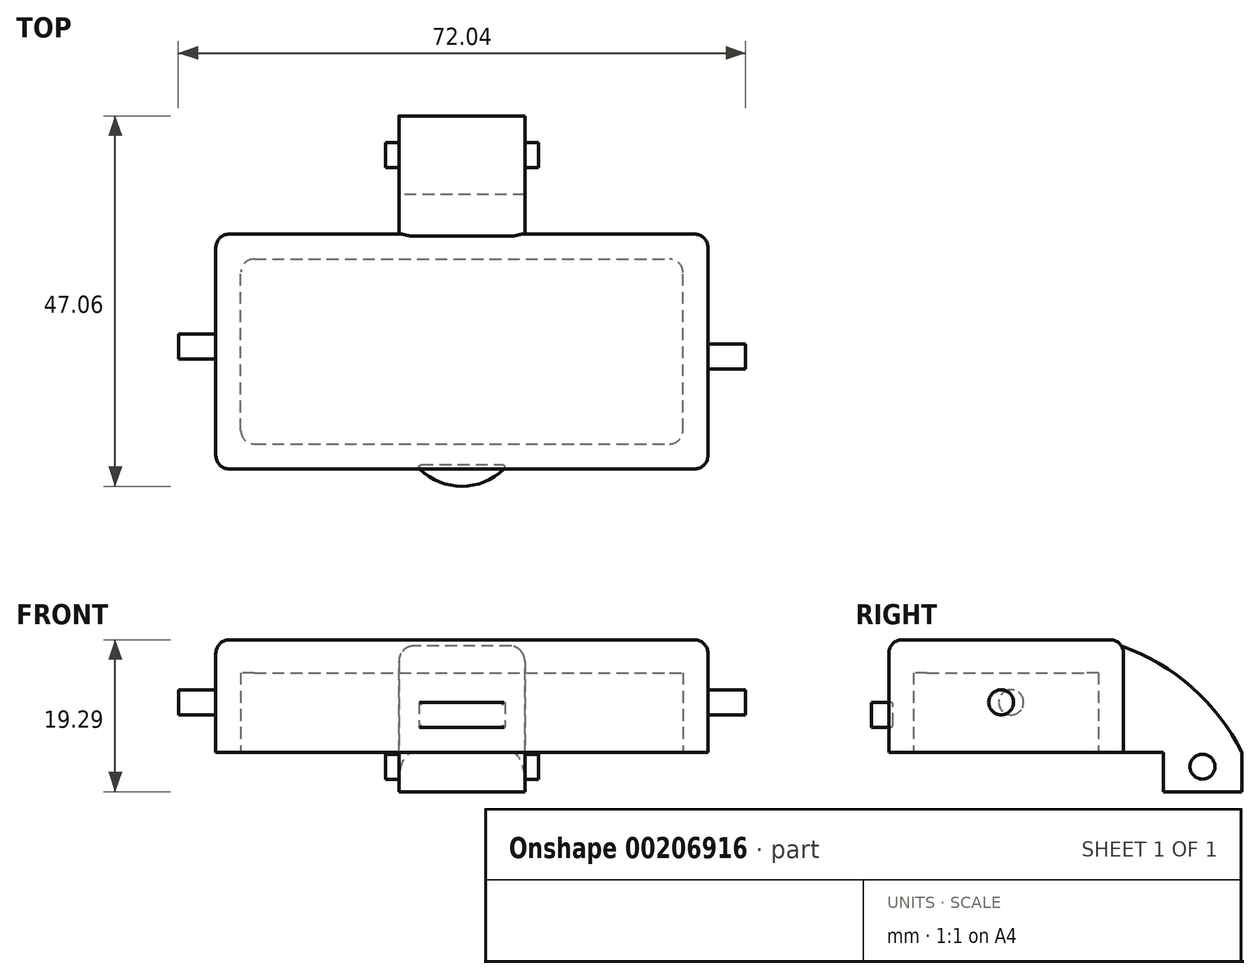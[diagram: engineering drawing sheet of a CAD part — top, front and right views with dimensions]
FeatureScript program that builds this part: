
annotation { "Feature Type Name" : "Feature", "Feature Type Description" : "" }
export const myFeature = defineFeature(function(context is Context, id is Id, definition is map)
    precondition{}
    {
        {
            var Q0;
            Q0=qCreatedBy(makeId("Top.planeOp"),FACE);
            var sketch = newSketch(context, id + "F0", { "sketchPlane" : qUnion([Q0])});
            skLineSegment(sketch, "E0.bottom", {"start": v(-31.25, 14.92) * mm, "end": v(31.25, 14.92) * mm});
            skLineSegment(sketch, "E0.top", {"start": v(-31.25, -14.92) * mm, "end": v(31.25, -14.92) * mm});
            skLineSegment(sketch, "E0.left", {"start": v(-31.25, 14.92) * mm, "end": v(-31.25, -14.92) * mm});
            skLineSegment(sketch, "E0.right", {"start": v(31.25, 14.92) * mm, "end": v(31.25, -14.92) * mm});
            skPoint(sketch, "E0.middle", {"position": v(0, 0) * mm});
            skSolve(sketch);
        }
        {
            var Q0;
            Q0=qSketchRegion(id+"F0",true);
            extrude(context, id + "F1", {"entities" : qUnion([Q0]), "depth" : 14.29 * mm});
        }
        {
            var Q0;
            Q0=qCreatedBy(makeId("Top.planeOp"),FACE);
            cPlane(context, id + "F2", {"entities" : qUnion([Q0]), "cplaneType" : CPlaneType.OFFSET, "offset" : 3.17 * mm, "width" : 152.4 * mm, "height" : 152.4 * mm});
        }
        {
            var Q0;
            Q0=qCreatedBy(id+"F2.planeOp",FACE);
            var sketch = newSketch(context, id + "F3", { "sketchPlane" : qUnion([Q0])});
            skPoint(sketch, "E1", {"position": v(-5.85, -14.38) * mm});
            skPoint(sketch, "E2", {"position": v(5.85, -14.38) * mm});
            skArc(sketch, "E3", {"start": v(-5.85, -14.38) * mm, "mid": v(0, -17.12) * mm, "end": v(5.85, -14.38) * mm});
            skLineSegment(sketch, "E4", {"start": v(-5.85, -14.38) * mm, "end": v(5.85, -14.38) * mm});
            skSolve(sketch);
        }
        {
            var Q0;
            Q0=qSketchRegion(id+"F3",true);
            extrude(context, id + "F4", {"entities" : qUnion([Q0]), "depth" : 3.17 * mm});
        }
        {
            var Q0;
            {var subQ0=sQuery(id+"F3.wireOp",EDGE,"E4");var subQ1=sQuery(id+"F3.wireOp",EDGE,"E3");Q0=makeQuery(id+"F4.opExtrude","SWEPT_EDGE",EDGE,{"disambiguationData":[OSD([subQ1,subQ0]),TDD([makeQuery(id+"F3.imprint","INTERSECT",VERTEX,{"disambiguationData":[OD(1.0)],"derivedFrom":[subQ1,subQ0]})])]});}
            var Q1;
            {var subQ0=sQuery(id+"F3.wireOp",EDGE,"E4");var subQ1=sQuery(id+"F3.wireOp",EDGE,"E3");Q1=makeQuery(id+"F4.opExtrude","SWEPT_EDGE",EDGE,{"disambiguationData":[OSD([subQ1,subQ0]),TDD([makeQuery(id+"F3.imprint","INTERSECT",VERTEX,{"disambiguationData":[OD(0.0)],"derivedFrom":[subQ1,subQ0]})])]});}
            var Q2;
            Q2=makeQuery(id+"F4.opExtrude","CAP_EDGE",EDGE,{"disambiguationData":[OSD([sQuery(id+"F3.wireOp",EDGE,"E4")])],"isStart":false});
            var Q3;
            Q3=makeQuery(id+"F4.opExtrude","CAP_EDGE",EDGE,{"disambiguationData":[OSD([sQuery(id+"F3.wireOp",EDGE,"E4")])],"isStart":true});
            fillet(context, id + "F5", {"entities" : qUnion([Q0, Q1, Q2, Q3]), "radius" : 0.32 * mm, "tangentPropagation" : true, "allowEdgeOverflow" : false});
        }
        {
            var Q0;
            Q0=makeQuery(id+"F1.opExtrude","SWEPT_EDGE",EDGE,{"disambiguationData":[OSD([sQuery(id+"F0.wireOp",EDGE,"E0.top"),sQuery(id+"F0.wireOp",EDGE,"E0.left")])]});
            var Q1;
            Q1=makeQuery(id+"F1.opExtrude","SWEPT_EDGE",EDGE,{"disambiguationData":[OSD([sQuery(id+"F0.wireOp",EDGE,"E0.top"),sQuery(id+"F0.wireOp",EDGE,"E0.right")])]});
            var Q2;
            Q2=makeQuery(id+"F1.opExtrude","SWEPT_EDGE",EDGE,{"disambiguationData":[OSD([sQuery(id+"F0.wireOp",EDGE,"E0.bottom"),sQuery(id+"F0.wireOp",EDGE,"E0.right")])]});
            var Q3;
            Q3=makeQuery(id+"F1.opExtrude","SWEPT_EDGE",EDGE,{"disambiguationData":[OSD([sQuery(id+"F0.wireOp",EDGE,"E0.bottom"),sQuery(id+"F0.wireOp",EDGE,"E0.left")])]});
            var Q4;
            Q4=makeQuery(id+"F1.opExtrude","CAP_FACE",FACE,{"disambiguationData":[OSD([sQuery(id+"F0.wireOp",EDGE,"E0.bottom"),sQuery(id+"F0.wireOp",EDGE,"E0.top"),sQuery(id+"F0.wireOp",EDGE,"E0.left"),sQuery(id+"F0.wireOp",EDGE,"E0.right")])],"isStart":false});
            fillet(context, id + "F6", {"entities" : qUnion([Q0, Q1, Q2, Q3, Q4]), "radius" : 1.71 * mm, "tangentPropagation" : true, "allowEdgeOverflow" : false});
        }
        {
            var Q0;
            Q0=makeQuery(id+"F1.opExtrude","CAP_FACE",FACE,{"disambiguationData":[OSD([sQuery(id+"F0.wireOp",EDGE,"E0.bottom"),sQuery(id+"F0.wireOp",EDGE,"E0.top"),sQuery(id+"F0.wireOp",EDGE,"E0.left"),sQuery(id+"F0.wireOp",EDGE,"E0.right")])],"isStart":true});
            var sketch = newSketch(context, id + "F7", { "sketchPlane" : qUnion([Q0])});
            skLineSegment(sketch, "E5.bottom", {"start": v(-28.08, 11.75) * mm, "end": v(28.08, 11.75) * mm});
            skLineSegment(sketch, "E5.top", {"start": v(-28.08, -11.75) * mm, "end": v(28.08, -11.75) * mm});
            skLineSegment(sketch, "E5.left", {"start": v(-28.08, 11.75) * mm, "end": v(-28.08, -11.75) * mm});
            skLineSegment(sketch, "E5.right", {"start": v(28.08, 11.75) * mm, "end": v(28.08, -11.75) * mm});
            skSolve(sketch);
        }
        {
            var Q0;
            Q0=makeQuery(id+"F7.imprint","IMPRINT",FACE,{"disambiguationData":[TD([[makeQuery(id+"F7.imprint","IMPRINT",EDGE,{"derivedFrom":sQuery(id+"F7.wireOp",EDGE,"E5.bottom")}),-1.0]])]});
            extrude(context, id + "F8", {"entities" : qUnion([Q0]), "operationType" : NewBodyOperationType.REMOVE, "oppositeDirection" : true, "depth" : 10.1 * mm});
        }
        {
            var Q0;
            Q0=makeQuery(id+"F8.boolean.opBoolean","COPY",EDGE,{"derivedFrom":makeQuery(id+"F8.opExtrude","SWEPT_EDGE",EDGE,{"disambiguationData":[OSD([sQuery(id+"F7.wireOp",EDGE,"E5.top"),sQuery(id+"F7.wireOp",EDGE,"E5.left")])]})});
            var Q1;
            Q1=makeQuery(id+"F8.boolean.opBoolean","COPY",EDGE,{"derivedFrom":makeQuery(id+"F8.opExtrude","SWEPT_EDGE",EDGE,{"disambiguationData":[OSD([sQuery(id+"F7.wireOp",EDGE,"E5.bottom"),sQuery(id+"F7.wireOp",EDGE,"E5.left")])]})});
            var Q2;
            Q2=makeQuery(id+"F8.boolean.opBoolean","COPY",EDGE,{"derivedFrom":makeQuery(id+"F8.opExtrude","SWEPT_EDGE",EDGE,{"disambiguationData":[OSD([sQuery(id+"F7.wireOp",EDGE,"E5.bottom"),sQuery(id+"F7.wireOp",EDGE,"E5.right")])]})});
            var Q3;
            Q3=makeQuery(id+"F8.boolean.opBoolean","COPY",EDGE,{"derivedFrom":makeQuery(id+"F8.opExtrude","SWEPT_EDGE",EDGE,{"disambiguationData":[OSD([sQuery(id+"F7.wireOp",EDGE,"E5.top"),sQuery(id+"F7.wireOp",EDGE,"E5.right")])]})});
            fillet(context, id + "F9", {"entities" : qUnion([Q0, Q1, Q2, Q3]), "radius" : 1.71 * mm, "tangentPropagation" : true, "allowEdgeOverflow" : false});
        }
        {
            var Q0;
            Q0=makeQuery(id+"F1.opExtrude","SWEPT_FACE",FACE,{"disambiguationData":[OSD([sQuery(id+"F0.wireOp",EDGE,"E0.right")])]});
            var sketch = newSketch(context, id + "F10", { "sketchPlane" : qUnion([Q0])});
            skCircle(sketch, "E6", {"center": v(-0.63, 6.35) * mm, "radius": 1.59 * mm});
            skSolve(sketch);
        }
        {
            var Q0;
            Q0=makeQuery(id+"F10.imprint","IMPRINT",FACE,{"disambiguationData":[TD([[makeQuery(id+"F10.imprint","IMPRINT",EDGE,{"derivedFrom":sQuery(id+"F10.wireOp",EDGE,"E6")}),1.0]])]});
            extrude(context, id + "F11", {"entities" : qUnion([Q0]), "operationType" : NewBodyOperationType.ADD, "depth" : 4.76 * mm});
        }
        {
            var Q0;
            Q0=makeQuery(id+"F1.opExtrude","SWEPT_FACE",FACE,{"disambiguationData":[OSD([sQuery(id+"F0.wireOp",EDGE,"E0.left")])]});
            var sketch = newSketch(context, id + "F12", { "sketchPlane" : qUnion([Q0])});
            skCircle(sketch, "E7", {"center": v(-0.63, 6.35) * mm, "radius": 1.59 * mm});
            skSolve(sketch);
        }
        {
            var Q0;
            Q0=makeQuery(id+"F12.imprint","IMPRINT",FACE,{"disambiguationData":[TD([[makeQuery(id+"F12.imprint","IMPRINT",EDGE,{"derivedFrom":sQuery(id+"F12.wireOp",EDGE,"E7")}),1.0]])]});
            extrude(context, id + "F13", {"entities" : qUnion([Q0]), "operationType" : NewBodyOperationType.ADD, "depth" : 4.76 * mm});
        }
        {
            var Q0;
            Q0=qCreatedBy(makeId("Right.planeOp"),FACE);
            var sketch = newSketch(context, id + "F14", { "sketchPlane" : qUnion([Q0])});
            skPoint(sketch, "E8", {"position": v(11.94, 14.29) * mm});
            skLineSegment(sketch, "E9", {"start": v(11.94, 0) * mm, "end": v(19.94, 0) * mm});
            skLineSegment(sketch, "E10", {"start": v(19.94, 0) * mm, "end": v(19.94, -5) * mm});
            skLineSegment(sketch, "E11", {"start": v(19.94, -5) * mm, "end": v(29.94, -5) * mm});
            skLineSegment(sketch, "E12", {"start": v(29.94, -5) * mm, "end": v(29.94, 0) * mm});
            skArc(sketch, "E13", {"start": v(29.94, 0) * mm, "mid": v(22.53, 9.15) * mm, "end": v(11.94, 14.29) * mm});
            skLineSegment(sketch, "E14", {"start": v(11.94, 14.29) * mm, "end": v(11.94, 0) * mm});
            skSolve(sketch);
        }
        {
            var Q0;
            Q0=makeQuery(id+"F14.imprint","IMPRINT",FACE,{"disambiguationData":[TD([[makeQuery(id+"F14.imprint","IMPRINT",EDGE,{"derivedFrom":sQuery(id+"F14.wireOp",EDGE,"E9")}),1.0]])]});
            extrude(context, id + "F15", {"entities" : qUnion([Q0]), "operationType" : NewBodyOperationType.ADD, "endBound" : BoundingType.SYMMETRIC, "depth" : 16 * mm});
        }
        {
            var Q0;
            Q0=makeQuery(id+"F15.opExtrude","CAP_EDGE",EDGE,{"disambiguationData":[OSD([sQuery(id+"F14.wireOp",EDGE,"E13")])],"isStart":false});
            var Q1;
            Q1=makeQuery(id+"F15.opExtrude","CAP_EDGE",EDGE,{"disambiguationData":[OSD([sQuery(id+"F14.wireOp",EDGE,"E13")])],"isStart":true});
            fillet(context, id + "F16", {"entities" : qUnion([Q0, Q1]), "radius" : 1.71 * mm, "tangentPropagation" : true, "allowEdgeOverflow" : false});
        }
        {
            var Q0;
            Q0=makeQuery(id+"F15.opExtrude","CAP_FACE",FACE,{"disambiguationData":[OSD([sQuery(id+"F14.wireOp",EDGE,"E9"),sQuery(id+"F14.wireOp",EDGE,"E10"),sQuery(id+"F14.wireOp",EDGE,"E11"),sQuery(id+"F14.wireOp",EDGE,"E12"),sQuery(id+"F14.wireOp",EDGE,"E13"),sQuery(id+"F14.wireOp",EDGE,"E14")])],"isStart":false});
            var sketch = newSketch(context, id + "F17", { "sketchPlane" : qUnion([Q0])});
            skCircle(sketch, "E15", {"center": v(24.94, -1.82) * mm, "radius": 1.59 * mm});
            skSolve(sketch);
        }
        {
            var Q0;
            Q0=makeQuery(id+"F17.imprint","IMPRINT",FACE,{"disambiguationData":[TD([[makeQuery(id+"F17.imprint","IMPRINT",EDGE,{"derivedFrom":sQuery(id+"F17.wireOp",EDGE,"E15")}),1.0]])]});
            extrude(context, id + "F18", {"entities" : qUnion([Q0]), "operationType" : NewBodyOperationType.ADD, "depth" : 1.71 * mm});
        }
        {
            var Q0;
            Q0=makeQuery(id+"F15.opExtrude","CAP_FACE",FACE,{"disambiguationData":[OSD([sQuery(id+"F14.wireOp",EDGE,"E9"),sQuery(id+"F14.wireOp",EDGE,"E10"),sQuery(id+"F14.wireOp",EDGE,"E11"),sQuery(id+"F14.wireOp",EDGE,"E12"),sQuery(id+"F14.wireOp",EDGE,"E13"),sQuery(id+"F14.wireOp",EDGE,"E14")])],"isStart":true});
            var sketch = newSketch(context, id + "F19", { "sketchPlane" : qUnion([Q0])});
            skCircle(sketch, "E16", {"center": v(-24.95, -1.82) * mm, "radius": 1.59 * mm});
            skSolve(sketch);
        }
        {
            var Q0;
            Q0=qSketchRegion(id+"F19",true);
            extrude(context, id + "F20", {"entities" : qUnion([Q0]), "operationType" : NewBodyOperationType.ADD, "depth" : 1.71 * mm});
        }
    });
